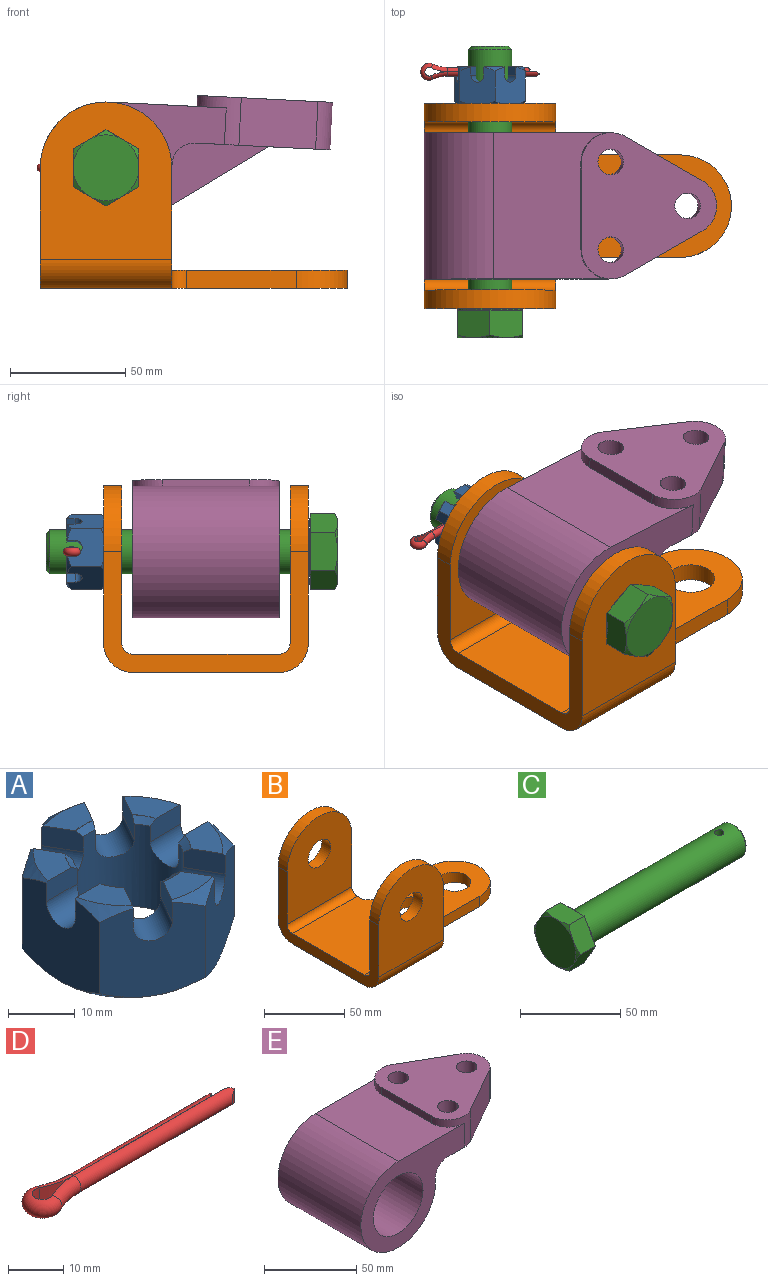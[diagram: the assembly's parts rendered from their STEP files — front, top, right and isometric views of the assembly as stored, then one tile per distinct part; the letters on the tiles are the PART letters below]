
ASSEMBLY  parts=5 mates=4
PART A: 64 faces, bbox 33x33x16.9 mm
  f0: cylinder r=8.33mm len=16.67mm, axis (0,0,1), area 599.6mm2, adj f8,f9,f10,f11,f12,f13,f14,f15
  f1: plane 28.58x28.58mm, normal (0,0,-1), area 356.3mm2, adj f32,f33,f34,f35,f36,f37,f51
  f2: plane 8.68x4.95mm, normal (0,0,1), area 30mm2, adj f12,f16,f41,f48
  f3: plane 7.52x6.81mm, normal (0,0,1), area 30mm2, adj f9,f13,f43,f49
  f4: plane 7.52x6.81mm, normal (0,0,1), area 30mm2, adj f8,f18,f39,f44
  f5: plane 7.52x6.81mm, normal (0,0,1), area 30mm2, adj f11,f15,f42,f46
  f6: plane 7.52x6.81mm, normal (0,0,1), area 30mm2, adj f10,f17,f40,f47
  f7: plane 8.68x4.95mm, normal (0,0,1), area 30mm2, adj f14,f19,f38,f45
  f8: plane 6.56x3.71mm, normal (0,-1,0), area 23.4mm2, adj f0,f4,f22,f26,f39,f44,f62,f63
  f9: plane 6.56x3.71mm, normal (0,1,0), area 23.4mm2, adj f0,f3,f22,f26,f43,f49,f52,f53
  f10: plane 6.56x3.71mm, normal (0,1,0), area 23.4mm2, adj f0,f6,f25,f27,f40,f47,f56,f57
  f11: plane 6.56x3.71mm, normal (0,-1,0), area 23.4mm2, adj f0,f5,f25,f27,f42,f46,f58,f59
  f12: plane 5.69x3.71mm, normal (0.87,0.5,0), area 23.4mm2, adj f0,f2,f23,f28,f41,f48,f54,f55
  f13: plane 5.69x3.71mm, normal (-0.87,-0.5,0), area 23.4mm2, adj f0,f3,f23,f28,f43,f49,f52,f53
  f14: plane 5.69x3.71mm, normal (-0.87,-0.5,0), area 23.4mm2, adj f0,f7,f20,f29,f38,f45,f60,f61
  f15: plane 5.69x3.71mm, normal (0.87,0.5,0), area 23.4mm2, adj f0,f5,f20,f29,f42,f46,f58,f59
  f16: plane 5.69x3.71mm, normal (-0.87,0.5,0), area 23.4mm2, adj f0,f2,f24,f30,f41,f48,f54,f55
  f17: plane 5.69x3.71mm, normal (0.87,-0.5,0), area 23.4mm2, adj f0,f6,f24,f30,f40,f47,f56,f57
  f18: plane 5.69x3.71mm, normal (-0.87,0.5,0), area 23.4mm2, adj f0,f4,f21,f31,f39,f44,f62,f63
  f19: plane 5.69x3.71mm, normal (0.87,-0.5,0), area 23.4mm2, adj f0,f7,f21,f31,f38,f45,f60,f61
  f20: plane 16.62x14.29mm, normal (-0.5,0.87,0), area 220.6mm2, adj f14,f15,f21,f25,f29,f32,f33,f38
  f21: plane 16.62x14.29mm, normal (0.5,0.87,0), area 220.6mm2, adj f18,f19,f20,f22,f31,f33,f34,f38
  f22: plane 16.63x16.51mm, normal (1,0,0), area 220.6mm2, adj f8,f9,f21,f23,f26,f34,f35,f39
  f23: plane 16.62x14.29mm, normal (0.5,-0.87,0), area 220.6mm2, adj f12,f13,f22,f24,f28,f35,f36,f41
  f24: plane 16.62x14.29mm, normal (-0.5,-0.87,0), area 220.6mm2, adj f16,f17,f23,f25,f30,f36,f37,f40
  f25: plane 16.63x16.51mm, normal (-1,0,0), area 220.6mm2, adj f10,f11,f20,f24,f27,f32,f37,f40
  f26: cylinder r=3.05mm len=6.53mm, axis (1,0,0), area 59.8mm2, adj f0,f8,f9,f22
  f27: cylinder r=3.05mm len=6.53mm, axis (1,0,0), area 59.8mm2, adj f0,f10,f11,f25
  f28: cylinder r=3.05mm len=8.7mm, axis (-0.5,0.87,0), area 59.8mm2, adj f0,f12,f13,f23
  f29: cylinder r=3.05mm len=8.7mm, axis (-0.5,0.87,0), area 59.8mm2, adj f0,f14,f15,f20
  f30: cylinder r=3.05mm len=8.7mm, axis (0.5,0.87,0), area 59.8mm2, adj f0,f16,f17,f24
  f31: cylinder r=3.05mm len=8.7mm, axis (0.5,0.87,0), area 59.8mm2, adj f0,f18,f19,f21
  f32: cone r=14.29mm half-angle=49.2deg, axis (0,0,1), area 14.5mm2, adj f1,f20,f25
  f33: cone r=14.29mm half-angle=49.2deg, axis (0,0,1), area 14.5mm2, adj f1,f20,f21
  f34: cone r=14.29mm half-angle=49.2deg, axis (0,0,1), area 14.5mm2, adj f1,f21,f22
  f35: cone r=14.29mm half-angle=49.2deg, axis (0,0,1), area 14.5mm2, adj f1,f22,f23
  f36: cone r=14.29mm half-angle=49.2deg, axis (0,0,1), area 14.5mm2, adj f1,f23,f24
  f37: cone r=14.29mm half-angle=49.2deg, axis (0,0,1), area 14.5mm2, adj f1,f24,f25
  f38: cone r=14.29mm half-angle=49.2deg, axis (0,0,-1), area 13.6mm2, adj f7,f14,f19,f20,f21
  f39: cone r=14.29mm half-angle=49.2deg, axis (0,0,-1), area 13.6mm2, adj f4,f8,f18,f21,f22
  f40: cone r=14.29mm half-angle=49.2deg, axis (0,0,-1), area 13.6mm2, adj f6,f10,f17,f24,f25
  f41: cone r=14.29mm half-angle=49.2deg, axis (0,0,-1), area 13.6mm2, adj f2,f12,f16,f23,f24
  f42: cone r=14.29mm half-angle=49.2deg, axis (0,0,-1), area 13.6mm2, adj f5,f11,f15,f20,f25
  f43: cone r=14.29mm half-angle=49.2deg, axis (0,0,-1), area 13.6mm2, adj f3,f9,f13,f22,f23
  f44: cone r=8.21mm half-angle=55deg, axis (0,0,1), area 0.1mm2, adj f4,f8,f18,f63
  f45: cone r=8.21mm half-angle=55deg, axis (0,0,1), area 0.1mm2, adj f7,f14,f19,f60
  f46: cone r=8.21mm half-angle=55deg, axis (0,0,1), area 0.1mm2, adj f5,f11,f15,f58
  f47: cone r=8.21mm half-angle=55deg, axis (0,0,1), area 0.1mm2, adj f6,f10,f17,f56
  f48: cone r=8.21mm half-angle=55deg, axis (0,0,1), area 0.1mm2, adj f2,f12,f16,f54
  f49: cone r=8.21mm half-angle=55deg, axis (0,0,1), area 0.1mm2, adj f3,f9,f13,f52
  f50: cone r=9.53mm half-angle=55deg, axis (0,0,-1), area 81.6mm2, adj f0,f51
  f51: cylinder r=9.53mm len=19.05mm, axis (0,0,1), area 1.5mm2, adj f1,f50
  f52: cone r=9.53mm half-angle=55deg, axis (0,0,-1), area 0.1mm2, adj f9,f13,f49,f53
  f53: cone r=8.33mm half-angle=55deg, axis (0,0,1), area 4.5mm2, adj f0,f9,f13,f52
  f54: cone r=9.53mm half-angle=55deg, axis (0,0,-1), area 0.1mm2, adj f12,f16,f48,f55
  f55: cone r=8.33mm half-angle=55deg, axis (0,0,1), area 4.5mm2, adj f0,f12,f16,f54
  f56: cone r=9.53mm half-angle=55deg, axis (0,0,-1), area 0.1mm2, adj f10,f17,f47,f57
  f57: cone r=8.33mm half-angle=55deg, axis (0,0,1), area 4.5mm2, adj f0,f10,f17,f56
  f58: cone r=9.53mm half-angle=55deg, axis (0,0,-1), area 0.1mm2, adj f11,f15,f46,f59
  f59: cone r=8.33mm half-angle=55deg, axis (0,0,1), area 4.5mm2, adj f0,f11,f15,f58
  f60: cone r=9.53mm half-angle=55deg, axis (0,0,-1), area 0.1mm2, adj f14,f19,f45,f61
  f61: cone r=8.33mm half-angle=55deg, axis (0,0,1), area 4.5mm2, adj f0,f14,f19,f60
  f62: cone r=8.33mm half-angle=55deg, axis (0,0,1), area 4.5mm2, adj f0,f8,f18,f63
  f63: cone r=9.53mm half-angle=55deg, axis (0,0,-1), area 0.1mm2, adj f8,f18,f44,f62
PART B: 24 faces, bbox 133.4x88.9x81 mm
  f0: plane 52.39x15.88mm, normal (1,0,0), area 449.1mm2, adj f1,f6,f7,f8,f9,f10,f15,f23
  f1: plane 133.35x63.5mm, normal (0,0,-1), area 6151.6mm2, adj f0,f2,f10,f11,f12,f13,f14,f17
  f2: cylinder r=12.7mm len=57.15mm, axis (-1,0,0), area 1140.1mm2, adj f1,f3,f11,f12
  f3: plane 68.26x57.15mm, normal (0,1,0), area 3241.4mm2, adj f2,f11,f12,f16,f21
  f4: plane 68.26x57.15mm, normal (0,-1,0), area 3241.4mm2, adj f5,f11,f12,f16,f21
  f5: cylinder r=4.76mm len=57.15mm, axis (-1,0,0), area 427.5mm2, adj f4,f6,f11,f12
  f6: plane 133.35x63.5mm, normal (0,0,1), area 6151.6mm2, adj f0,f5,f7,f11,f12,f13,f14,f17
  f7: cylinder r=4.76mm len=57.15mm, axis (-1,0,0), area 427.5mm2, adj f0,f6,f8,f12
  f8: plane 68.26x57.15mm, normal (0,1,0), area 3241.4mm2, adj f0,f7,f12,f15,f20
  f9: plane 68.26x57.15mm, normal (0,-1,0), area 3241.4mm2, adj f0,f10,f12,f15,f20
  f10: cylinder r=12.7mm len=57.15mm, axis (-1,0,0), area 1140.1mm2, adj f0,f1,f9,f12
  f11: plane 52.39x15.88mm, normal (1,0,0), area 449.1mm2, adj f1,f2,f3,f4,f5,f6,f16,f22
  f12: plane 88.9x52.39mm, normal (-1,0,0), area 1351.8mm2, adj f1,f2,f3,f4,f5,f6,f7,f8
  f13: plane 47.63x7.94mm, normal (0,1,0), area 378mm2, adj f1,f6,f17,f22
  f14: plane 47.63x7.94mm, normal (0,-1,0), area 378mm2, adj f1,f6,f17,f23
  f15: cylinder r=28.57mm len=57.15mm, axis (0,-1,0), area 712.6mm2, adj f0,f8,f9,f12
  f16: cylinder r=28.57mm len=57.15mm, axis (0,1,0), area 712.6mm2, adj f3,f4,f11,f12
  f17: cylinder r=22.23mm len=44.45mm, axis (0,0,1), area 554.2mm2, adj f1,f6,f13,f14
  f18: cylinder r=10.33mm len=20.65mm, axis (0,0,1), area 514.9mm2, adj f1,f6
  f19: cylinder r=10.33mm len=20.65mm, axis (0,0,1), area 514.9mm2, adj f1,f6
  f20: cylinder r=9.92mm len=19.85mm, axis (0,-1,0), area 494.9mm2, adj f8,f9
  f21: cylinder r=9.92mm len=19.85mm, axis (0,-1,0), area 494.9mm2, adj f3,f4
  f22: cylinder r=6.35mm len=7.94mm, axis (0,0,1), area 79.2mm2, adj f1,f6,f11,f13
  f23: cylinder r=6.35mm len=7.94mm, axis (0,0,-1), area 79.2mm2, adj f0,f1,f6,f14
PART C: 26 faces, bbox 126.6x33x33 mm
  f0: plane 28.58x28.58mm, normal (1,0,0), area 325.1mm2, adj f10,f24
  f1: cylinder r=9.53mm len=112.28mm, axis (-1,0,0), area 6683.8mm2, adj f2,f24,f25
  f2: cone r=8.01mm half-angle=45deg, axis (-1,0,0), area 117.9mm2, adj f1,f3
  f3: plane 16.03x16.03mm, normal (1,0,0), area 201.7mm2, adj f2
  f4: plane 12.37x7.14mm, normal (1,0,0), area 11mm2, adj f10,f18,f23
  f5: plane 14.29x4.12mm, normal (1,0,0), area 11mm2, adj f10,f22,f23
  f6: plane 12.37x7.14mm, normal (1,0,0), area 11mm2, adj f10,f21,f22
  f7: plane 12.37x7.14mm, normal (1,0,0), area 11mm2, adj f10,f20,f21
  f8: plane 14.29x4.12mm, normal (1,0,0), area 11mm2, adj f10,f19,f20
  f9: plane 12.37x7.14mm, normal (1,0,0), area 11mm2, adj f10,f18,f19
  f10: cylinder r=14.29mm len=28.58mm, axis (-1,0,0), area 34.2mm2, adj f0,f4,f5,f6,f7,f8,f9
  f11: plane 28.58x28.58mm, normal (-1,0,0), area 641.3mm2, adj f12,f13,f14,f15,f16,f17
  f12: cone r=14.29mm half-angle=60deg, axis (1,0,0), area 12.7mm2, adj f11,f22,f23
  f13: cone r=14.29mm half-angle=60deg, axis (1,0,0), area 12.7mm2, adj f11,f21,f22
  f14: cone r=14.29mm half-angle=60deg, axis (1,0,0), area 12.7mm2, adj f11,f20,f21
  f15: cone r=14.29mm half-angle=60deg, axis (1,0,0), area 12.7mm2, adj f11,f19,f20
  f16: cone r=14.29mm half-angle=60deg, axis (1,0,0), area 12.7mm2, adj f11,f18,f23
  f17: cone r=14.29mm half-angle=60deg, axis (1,0,0), area 12.7mm2, adj f11,f18,f19
  f18: plane 16.51x11.89mm, normal (0,0,-1), area 188.9mm2, adj f4,f9,f16,f17,f19,f23
  f19: plane 14.29x11.89mm, normal (0,-0.87,-0.5), area 188.9mm2, adj f8,f9,f15,f17,f18,f20
  f20: plane 14.29x11.89mm, normal (0,-0.87,0.5), area 188.9mm2, adj f7,f8,f14,f15,f19,f21
  f21: plane 16.51x11.89mm, normal (0,0,1), area 188.9mm2, adj f6,f7,f13,f14,f20,f22
  f22: plane 14.29x11.89mm, normal (0,0.87,0.5), area 188.9mm2, adj f5,f6,f12,f13,f21,f23
  f23: plane 14.29x11.89mm, normal (0,0.87,-0.5), area 188.9mm2, adj f4,f5,f12,f16,f18,f22
  f24: torus R=10.03mm, axis (1,0,0), area 48.7mm2, adj f0,f1
  f25: cylinder r=2.38mm len=19.05mm, axis (0,0,1), area 285mm2, adj f1
PART D: 14 faces, bbox 52x8x3.7 mm
  f0: plane 38.67x3.7mm, normal (0,1,0), area 143.1mm2, adj f1,f2,f13
  f1: cylinder r=1.85mm len=40mm, axis (1,0,0), area 227.7mm2, adj f0,f3,f12,f13
  f2: cylinder r=16.37mm len=7.19mm, axis (0,0,-1), area 27.5mm2, adj f0,f3,f4
  f3: torus R=16.37mm, axis (0,0,-1), area 40.1mm2, adj f1,f2,f5
  f4: cylinder r=1.85mm len=3.7mm, axis (0,0,1), area 27.8mm2, adj f2,f5,f6
  f5: torus R=1.85mm, axis (0,0,1), area 71.2mm2, adj f3,f4,f7
  f6: cylinder r=16.37mm len=7.19mm, axis (0,0,-1), area 27.5mm2, adj f4,f7,f9
  f7: torus R=16.37mm, axis (0,0,-1), area 40.1mm2, adj f5,f6,f8
  f8: cylinder r=1.85mm len=36mm, axis (1,0,0), area 204.5mm2, adj f7,f9,f10,f11
  f9: plane 34.67x3.7mm, normal (0,-1,0), area 128.3mm2, adj f6,f8,f10
  f10: plane 3.7x1.33mm, normal (0.57,-0.82,0), area 5.7mm2, adj f8,f9,f11
  f11: plane 3.2x1.31mm, normal (0.58,0.82,0), area 3.6mm2, adj f8,f10
  f12: plane 3.2x1.31mm, normal (0.58,-0.82,0), area 3.6mm2, adj f1,f13
  f13: plane 3.7x1.33mm, normal (0.57,0.82,0), area 5.7mm2, adj f0,f1,f12
PART E: 23 faces, bbox 125.4x63.5x61.9 mm
  f0: plane 26.99x3.18mm, normal (1,0,0), area 85.7mm2, adj f1,f5,f9,f21
  f1: cylinder r=9.53mm len=26.99mm, axis (0,-1,0), area 403.8mm2, adj f0,f4,f9,f21
  f2: plane 63.5x50.8mm, normal (0,0,1), area 2488.6mm2, adj f5,f8,f9,f10,f11,f12
  f3: cylinder r=9.53mm len=26.99mm, axis (0,-1,0), area 403.8mm2, adj f4,f7,f8,f22
  f4: plane 63.5x58.75mm, normal (0,0,-1), area 2076.6mm2, adj f1,f3,f8,f9,f11,f12,f13,f14
  f5: cylinder r=28.57mm len=63.5mm, axis (0,-1,0), area 8284.9mm2, adj f0,f2,f7,f8,f9,f20,f21,f22
  f6: cylinder r=19.05mm len=63.5mm, axis (0,-1,0), area 7600.6mm2, adj f8,f9
  f7: plane 26.99x3.18mm, normal (1,0,0), area 85.7mm2, adj f3,f5,f8,f22
  f8: plane 79.38x57.15mm, normal (0,1,0), area 1972.6mm2, adj f2,f3,f4,f5,f6,f7,f11
  f9: plane 79.38x57.15mm, normal (0,-1,0), area 1972.6mm2, adj f0,f1,f2,f4,f5,f6,f12
  f10: plane 38.1x4.78mm, normal (-1,0,0), area 181.9mm2, adj f2,f11,f12,f16
  f11: cylinder r=12.7mm len=20.65mm, axis (0,0,-1), area 231.4mm2, adj f2,f4,f8,f10,f13,f16
  f12: cylinder r=12.7mm len=20.65mm, axis (0,0,-1), area 231.4mm2, adj f2,f4,f9,f10,f15,f16
  f13: plane 33.35x20.65mm, normal (0.5,0.87,0), area 793.1mm2, adj f4,f11,f14,f16
  f14: cylinder r=12.7mm len=22.06mm, axis (0,0,-1), area 551.7mm2, adj f4,f13,f15,f16
  f15: plane 33.35x20.65mm, normal (0.5,-0.87,0), area 793.1mm2, adj f4,f12,f14,f16
  f16: plane 63.5x58.75mm, normal (0,0,1), area 2309.8mm2, adj f10,f11,f12,f13,f14,f15,f17,f18
  f17: cylinder r=5.56mm len=20.65mm, axis (0,0,-1), area 721.7mm2, adj f4,f16
  f18: cylinder r=5.56mm len=20.65mm, axis (0,0,-1), area 721.7mm2, adj f4,f16
  f19: cylinder r=5.56mm len=20.65mm, axis (0,0,-1), area 721.7mm2, adj f4,f16
  f20: plane 53.86x36.38mm, normal (0.56,0,-0.83), area 619mm2, adj f4,f5,f21,f22
  f21: plane 53.86x36.38mm, normal (0,-1,0), area 591mm2, adj f0,f1,f4,f5,f20
  f22: plane 53.86x36.38mm, normal (0,1,0), area 591mm2, adj f3,f4,f5,f7,f20
PLACE A rot(axis=(-0.43,-0.64,-0.64),133.6deg) t=(-38.45,60.58,12.35)mm
PLACE B t=(-67.02,0.1,-32.1)mm fixed
PLACE C rot(axis=(-0.58,-0.58,0.58),120deg) t=(-38.45,-57.13,12.35)mm
PLACE D t=(-64.86,58.33,12.35)mm
PLACE E rot(axis=(0,1,0),2.9deg) t=(-38.45,0.1,12.35)mm
MATE revolute E.f5 <-> B.f15  axis (0,-1,0) through (-38.45,0.1,12.35)mm
MATE slider D.f8 <-> C.f25  axis (1,0,0) through (-38.75,58.33,12.35)mm
MATE slider C.f1 <-> B.f15  axis (0,1,0) through (-38.45,-44.35,12.35)mm
MATE cylindrical A.f0 <-> B.f15  axis (0,-1,0) through (-38.45,44.55,12.35)mm
